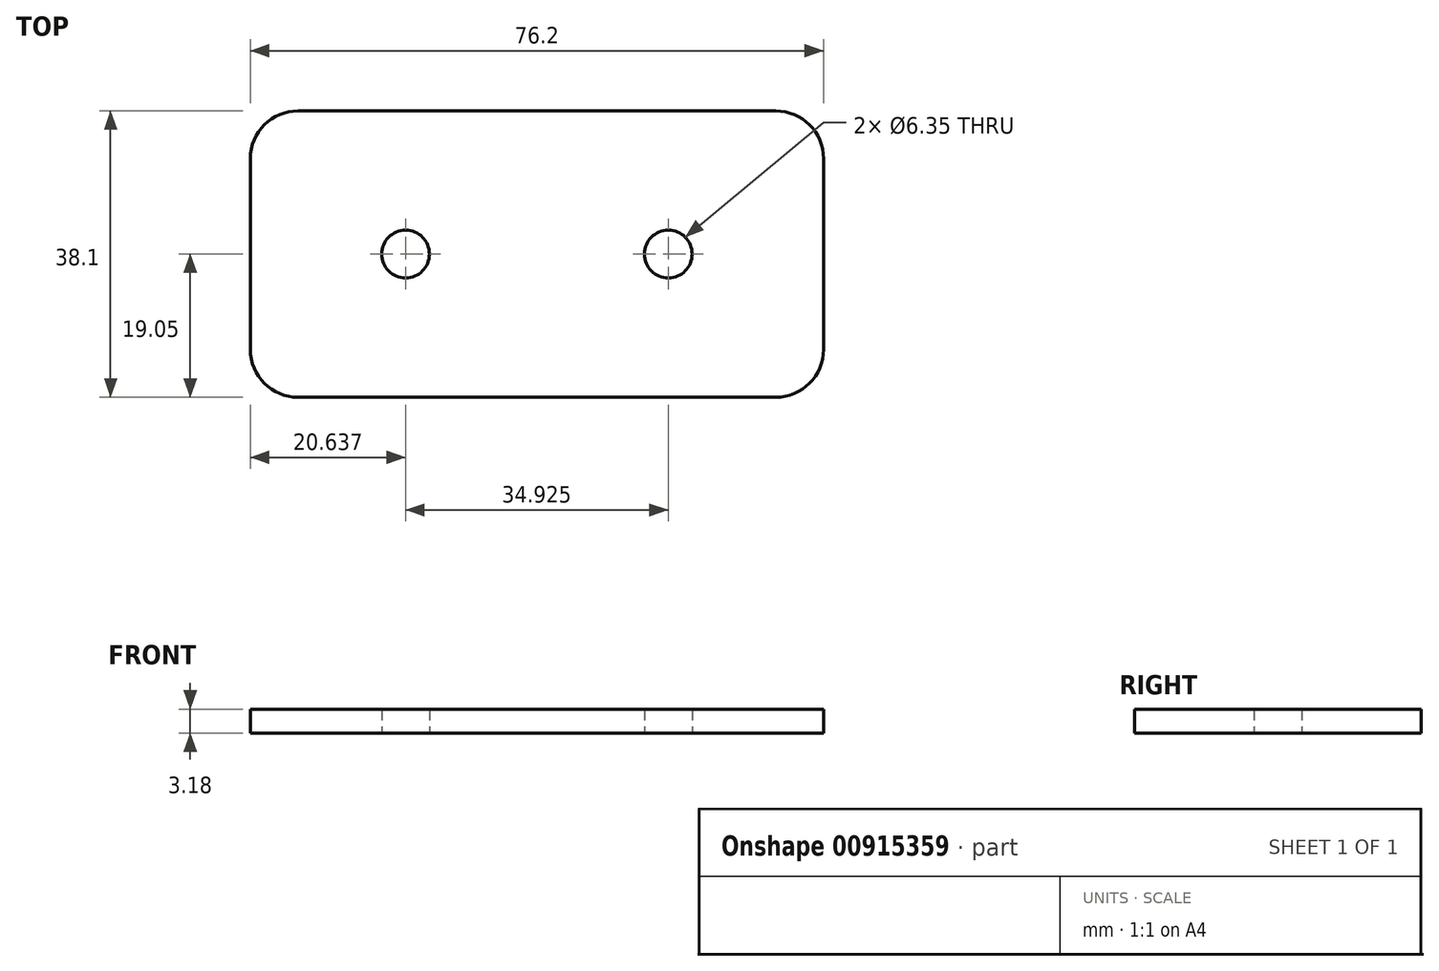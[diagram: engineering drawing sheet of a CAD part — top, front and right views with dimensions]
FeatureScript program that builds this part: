
annotation { "Feature Type Name" : "Feature", "Feature Type Description" : "" }
export const myFeature = defineFeature(function(context is Context, id is Id, definition is map)
    precondition{}
    {
        {
            var Q0;
            Q0=qCreatedBy(makeId("Top.planeOp"),FACE);
            var sketch = newSketch(context, id + "F0", { "sketchPlane" : qUnion([Q0])});
            skLineSegment(sketch, "E0.bottom", {"start": v(6.35, 0) * mm, "end": v(69.85, 0) * mm});
            skLineSegment(sketch, "E0.top", {"start": v(6.35, 38.1) * mm, "end": v(69.85, 38.1) * mm});
            skLineSegment(sketch, "E0.left", {"start": v(0, 6.35) * mm, "end": v(0, 31.75) * mm});
            skLineSegment(sketch, "E0.right", {"start": v(76.2, 6.35) * mm, "end": v(76.2, 31.75) * mm});
            skCircle(sketch, "E1", {"center": v(20.64, 19.05) * mm, "radius": 3.18 * mm});
            skCircle(sketch, "E2", {"center": v(55.56, 19.05) * mm, "radius": 3.17 * mm});
            skPoint(sketch, "E3.visualSharp", {"position": v(0, 38.1) * mm});
            skArc(sketch, "E3.filletArc", {"start": v(6.35, 38.1) * mm, "mid": v(1.86, 36.24) * mm, "end": v(0, 31.75) * mm});
            skPoint(sketch, "E4.visualSharp", {"position": v(0, 0) * mm});
            skArc(sketch, "E4.filletArc", {"start": v(0, 6.35) * mm, "mid": v(1.86, 1.86) * mm, "end": v(6.35, 0) * mm});
            skPoint(sketch, "E5.visualSharp", {"position": v(76.2, 38.1) * mm});
            skArc(sketch, "E5.filletArc", {"start": v(76.2, 31.75) * mm, "mid": v(74.34, 36.24) * mm, "end": v(69.85, 38.1) * mm});
            skPoint(sketch, "E6.visualSharp", {"position": v(76.2, 0) * mm});
            skArc(sketch, "E6.filletArc", {"start": v(69.85, 0) * mm, "mid": v(74.34, 1.86) * mm, "end": v(76.2, 6.35) * mm});
            skSolve(sketch);
        }
        {
            var Q0;
            Q0 = qSketchRegion(id + "F0", true);
            extrude(context, id + "F1", {"entities" : qUnion([Q0]), "depth" : 3.17 * mm, "offsetDistance" : 25.4 * mm});
        }
    });
